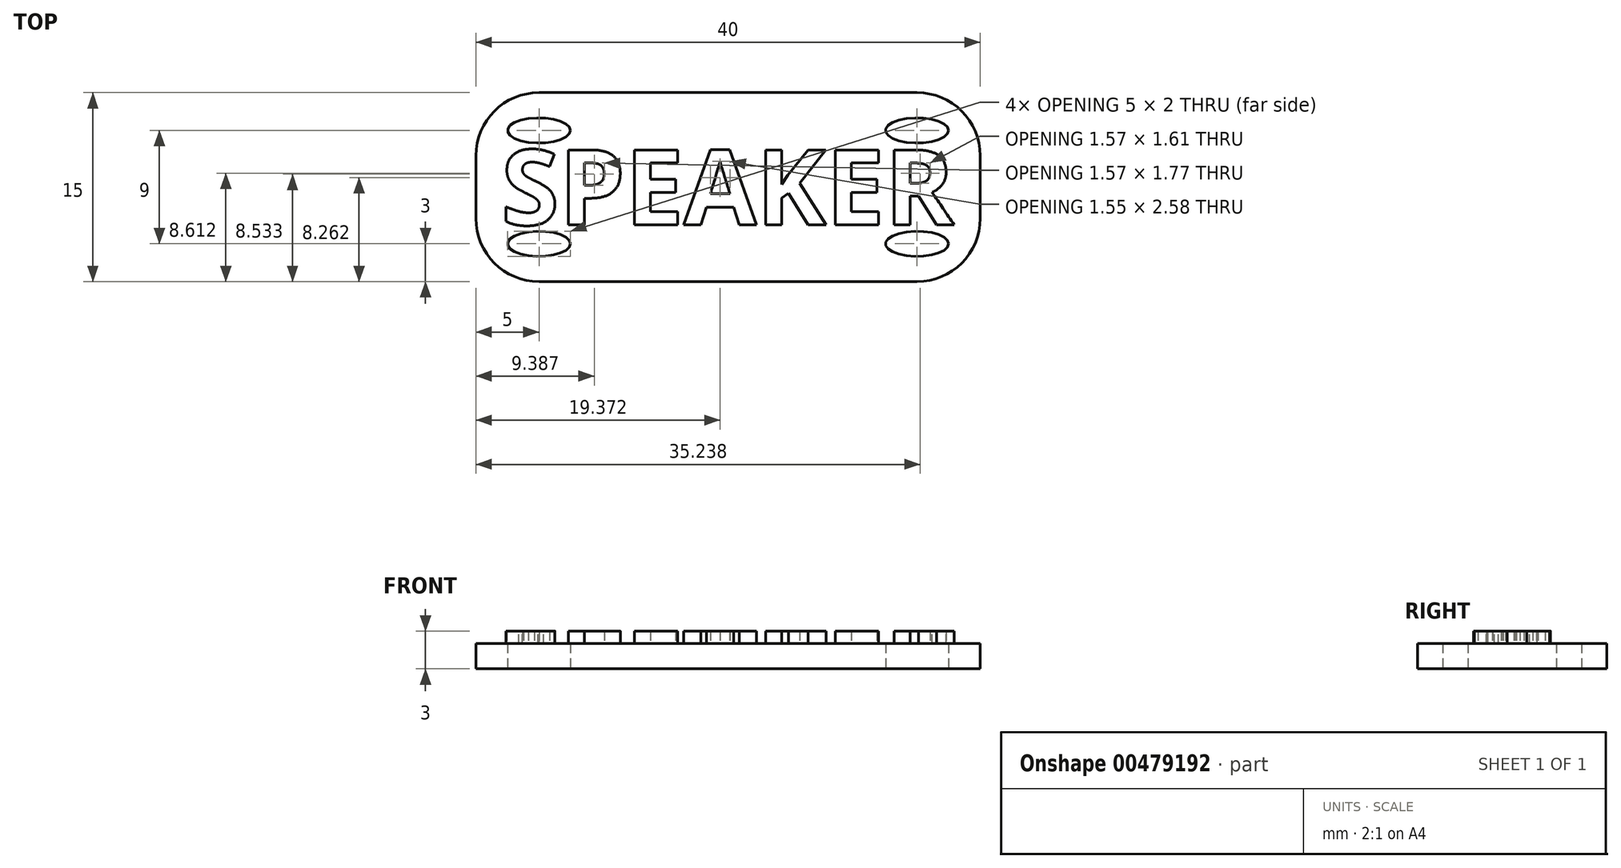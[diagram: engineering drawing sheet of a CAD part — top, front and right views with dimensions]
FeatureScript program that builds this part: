
annotation { "Feature Type Name" : "Feature", "Feature Type Description" : "" }
export const myFeature = defineFeature(function(context is Context, id is Id, definition is map)
    precondition{}
    {
        {
            var Q0;
            Q0=qCreatedBy(makeId("Top.planeOp"),FACE);
            var sketch = newSketch(context, id + "F0", { "sketchPlane" : qUnion([Q0])});
            skLineSegment(sketch, "E0.bottom", {"start": v(20, -7.5) * mm, "end": v(-20, -7.5) * mm});
            skLineSegment(sketch, "E0.top", {"start": v(20, 7.5) * mm, "end": v(-20, 7.5) * mm});
            skLineSegment(sketch, "E0.left", {"start": v(20, -7.5) * mm, "end": v(20, 7.5) * mm});
            skLineSegment(sketch, "E0.right", {"start": v(-20, -7.5) * mm, "end": v(-20, 7.5) * mm});
            skPoint(sketch, "E0.middle", {"position": v(0, 0) * mm});
            skLineSegment(sketch, "E1", {"start": v(-20, -4.5) * mm, "end": v(20, -4.5) * mm, "construction": true});
            skPoint(sketch, "E2", {"position": v(-15, -4.5) * mm});
            skEllipse(sketch, "E3", {"center": v(-15, -4.5) * mm, "majorRadius": 2.5 * mm, "minorRadius": 1 * mm, "majorAxis": v(1, 0)});
            skEllipse(sketch, "E4.1.0.0", {"center": v(15, -4.5) * mm, "majorRadius": 2.5 * mm, "minorRadius": 1 * mm, "majorAxis": v(1, 0)});
            skLineSegment(sketch, "E4.direction1", {"start": v(-15, -4.5) * mm, "end": v(15, -4.5) * mm, "construction": true});
            skLineSegment(sketch, "E5", {"start": v(20, 0) * mm, "end": v(-20, 0) * mm, "construction": true});
            skEllipse(sketch, "E6.MirrorC", {"center": v(15, 4.5) * mm, "majorRadius": 2.5 * mm, "minorRadius": 1 * mm, "majorAxis": v(1, 0)});
            skEllipse(sketch, "E7.MirrorC", {"center": v(-15, 4.5) * mm, "majorRadius": 2.5 * mm, "minorRadius": 1 * mm, "majorAxis": v(1, 0)});
            skSolve(sketch);
        }
        {
            var Q0;
            Q0=makeQuery(id+"F0.imprint","IMPRINT",FACE,{"disambiguationData":[TD([[makeQuery(id+"F0.imprint","IMPRINT",EDGE,{"derivedFrom":sQuery(id+"F0.wireOp",EDGE,"E0.bottom")}),-1.0]])]});
            extrude(context, id + "F1", {"entities" : qUnion([Q0]), "depth" : 2 * mm});
        }
        {
            var Q0;
            Q0=makeQuery(id+"F1.opExtrude","CAP_FACE",FACE,{"disambiguationData":[OSD([sQuery(id+"F0.wireOp",EDGE,"E0.bottom"),sQuery(id+"F0.wireOp",EDGE,"E0.top"),sQuery(id+"F0.wireOp",EDGE,"E0.left"),sQuery(id+"F0.wireOp",EDGE,"E0.right"),sQuery(id+"F0.wireOp",EDGE,"E3"),sQuery(id+"F0.wireOp",EDGE,"E4.1.0.0"),sQuery(id+"F0.wireOp",EDGE,"E6.MirrorC"),sQuery(id+"F0.wireOp",EDGE,"E7.MirrorC")])],"isStart":false});
            var sketch = newSketch(context, id + "F2", { "sketchPlane" : qUnion([Q0])});
            skText(sketch, "E8", { "text": "SPEAKER", "fontName": "OpenSans-Bold.ttf"});
            const initialGuessF2  = {"E8": [-0.018, -0.003, 1, 0, 0.006]};
            skSetInitialGuess(sketch, initialGuessF2);
            skSolve(sketch);
        }
        {
            var Q0;
            Q0=qSketchRegion(id+"F2",true);
            extrude(context, id + "F3", {"entities" : qUnion([Q0]), "depth" : 1 * mm});
        }
        {
            var Q0;
            Q0=makeQuery(id+"F1.opExtrude","SWEPT_EDGE",EDGE,{"disambiguationData":[OSD([sQuery(id+"F0.wireOp",EDGE,"E0.bottom"),sQuery(id+"F0.wireOp",EDGE,"E0.right")])]});
            var Q1;
            Q1=makeQuery(id+"F1.opExtrude","SWEPT_EDGE",EDGE,{"disambiguationData":[OSD([sQuery(id+"F0.wireOp",EDGE,"E0.bottom"),sQuery(id+"F0.wireOp",EDGE,"E0.left")])]});
            var Q2;
            Q2=makeQuery(id+"F1.opExtrude","SWEPT_EDGE",EDGE,{"disambiguationData":[OSD([sQuery(id+"F0.wireOp",EDGE,"E0.top"),sQuery(id+"F0.wireOp",EDGE,"E0.left")])]});
            var Q3;
            Q3=makeQuery(id+"F1.opExtrude","SWEPT_EDGE",EDGE,{"disambiguationData":[OSD([sQuery(id+"F0.wireOp",EDGE,"E0.top"),sQuery(id+"F0.wireOp",EDGE,"E0.right")])]});
            fillet(context, id + "F4", {"entities" : qUnion([Q0, Q1, Q2, Q3]), "radius" : 5 * mm, "tangentPropagation" : true, "allowEdgeOverflow" : false});
        }
    });
